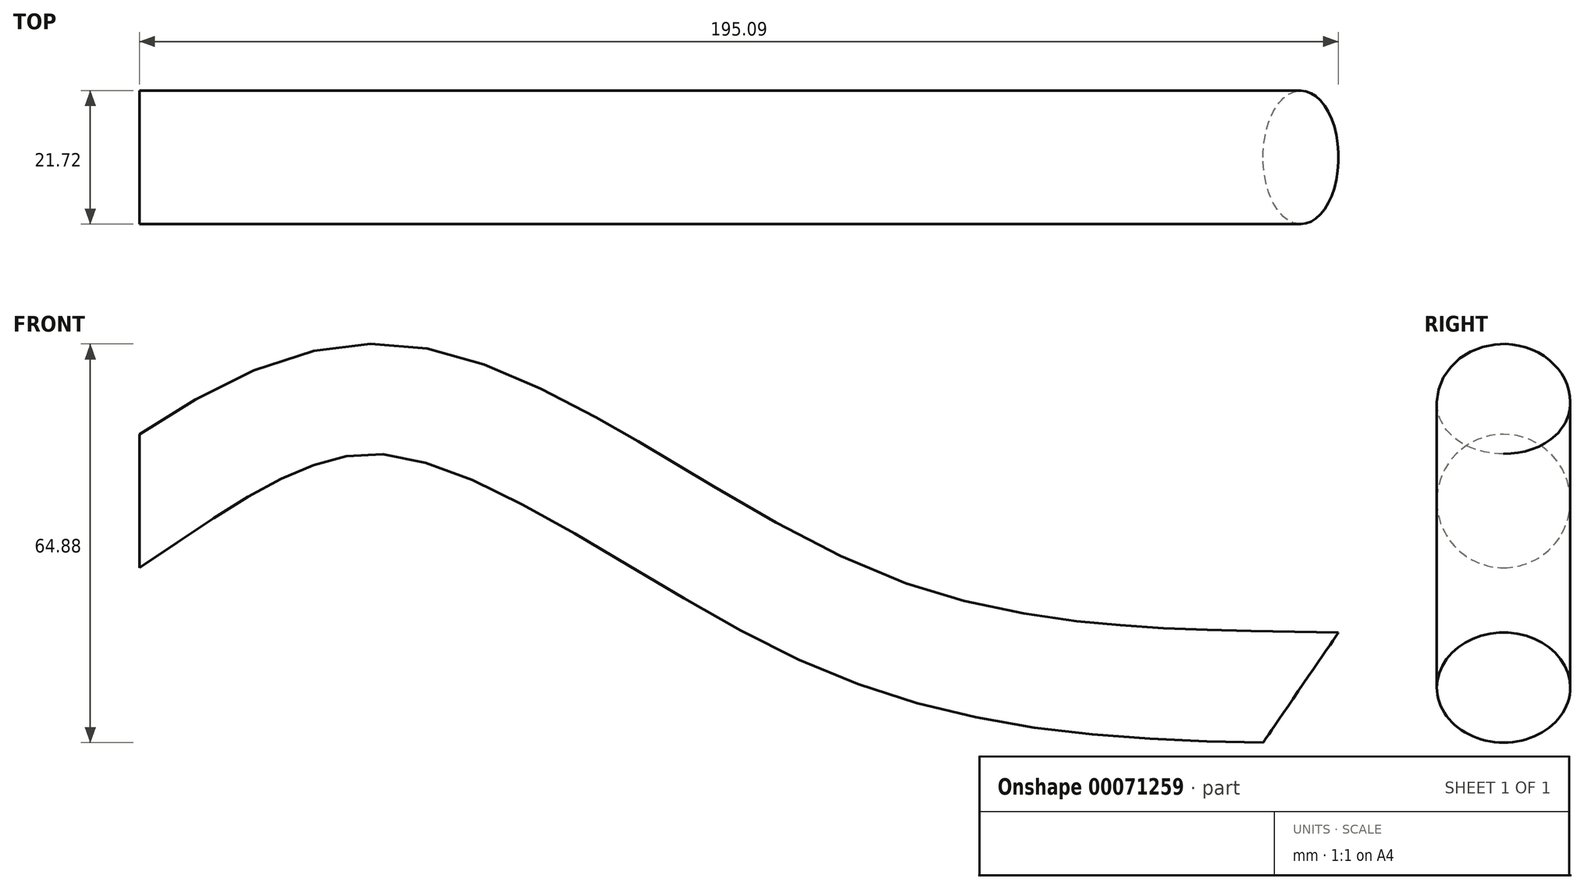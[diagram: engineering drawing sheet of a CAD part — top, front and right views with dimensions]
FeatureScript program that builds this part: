
annotation { "Feature Type Name" : "Feature", "Feature Type Description" : "" }
export const myFeature = defineFeature(function(context is Context, id is Id, definition is map)
    precondition{}
    {
        {
            var Q0;
            Q0=qCreatedBy(makeId("Right.planeOp"),FACE);
            var sketch = newSketch(context, id + "F0", { "sketchPlane" : qUnion([Q0])});
            skCircle(sketch, "E0", {"center": v(0, 0) * mm, "radius": 10.86 * mm});
            skSolve(sketch);
        }
        {
            var Q0;
            Q0=qCreatedBy(makeId("Front.planeOp"),FACE);
            var sketch = newSketch(context, id + "F1", { "sketchPlane" : qUnion([Q0])});
            skFitSpline(sketch, "E1", {"points": [v(0, 0) * mm, v(42.88, 15.86) * mm, v(114.55, -19) * mm, v(188.95, -30.35) * mm], "startDerivative": vector(145.76, 96.24) * mm, "endDerivative": vector(209.4, -3.6) * mm});
            skSolve(sketch);
        }
        {
            var Q0;
            Q0=makeQuery(id+"F0.imprint","IMPRINT",FACE,{"disambiguationData":[TD([[makeQuery(id+"F0.imprint","IMPRINT",EDGE,{"derivedFrom":sQuery(id+"F0.wireOp",EDGE,"E0")}),1.0]])]});
            var Q1;
            Q1=sQuery(id+"F1.wireOp",EDGE,"E1");
            sweep(context, id + "F2", {"profiles" : qUnion([Q0]), "path" : qUnion([Q1])});
        }
    });
